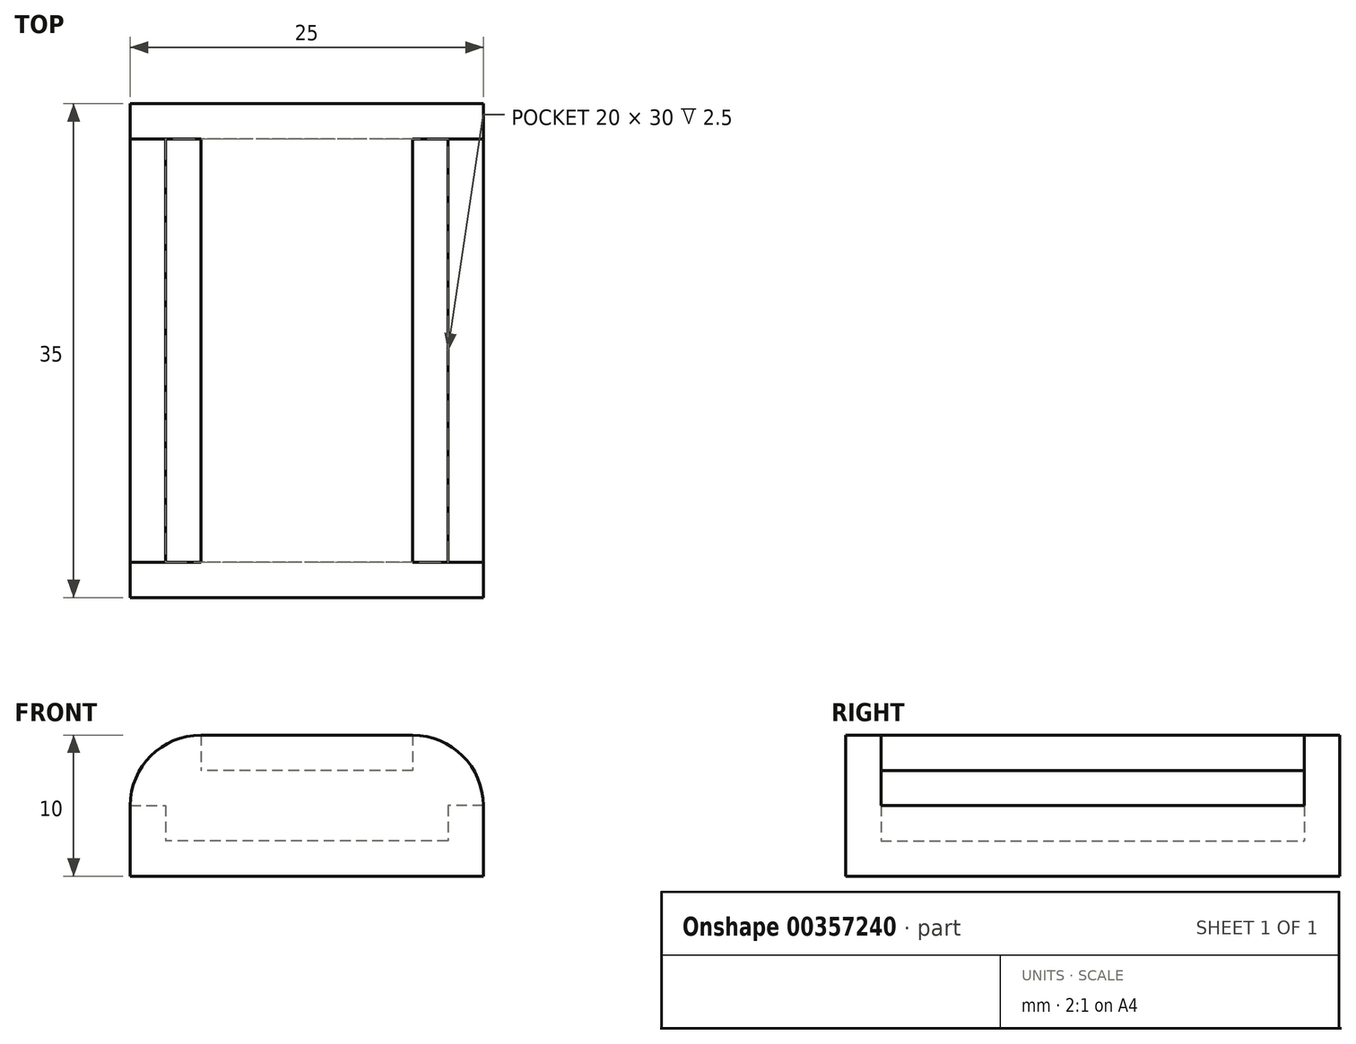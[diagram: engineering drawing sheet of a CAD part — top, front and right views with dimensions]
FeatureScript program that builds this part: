
annotation { "Feature Type Name" : "Feature", "Feature Type Description" : "" }
export const myFeature = defineFeature(function(context is Context, id is Id, definition is map)
    precondition{}
    {
        {
            var Q0;
            Q0=qCreatedBy(makeId("Top.planeOp"),FACE);
            var sketch = newSketch(context, id + "F0", { "sketchPlane" : qUnion([Q0])});
            skLineSegment(sketch, "E0.bottom", {"start": v(12.5, -17.5) * mm, "end": v(-12.5, -17.5) * mm});
            skLineSegment(sketch, "E0.top", {"start": v(12.5, 17.5) * mm, "end": v(-12.5, 17.5) * mm});
            skLineSegment(sketch, "E0.left", {"start": v(12.5, -17.5) * mm, "end": v(12.5, 17.5) * mm});
            skLineSegment(sketch, "E0.right", {"start": v(-12.5, -17.5) * mm, "end": v(-12.5, 17.5) * mm});
            skPoint(sketch, "E0.middle", {"position": v(0, 0) * mm});
            skSolve(sketch);
        }
        {
            var Q0;
            Q0 = qSketchRegion(id + "F0", true);
            extrude(context, id + "F1", {"entities" : qUnion([Q0]), "depth" : 5 * mm});
        }
        {
            var Q0;
            Q0=qCreatedBy(makeId("Top.planeOp"),FACE);
            var sketch = newSketch(context, id + "F2", { "sketchPlane" : qUnion([Q0])});
            skLineSegment(sketch, "E1.bottom", {"start": v(12.5, -17.5) * mm, "end": v(-12.5, -17.5) * mm});
            skLineSegment(sketch, "E1.top", {"start": v(12.5, 17.5) * mm, "end": v(-12.5, 17.5) * mm});
            skLineSegment(sketch, "E1.left", {"start": v(12.5, -17.5) * mm, "end": v(12.5, 17.5) * mm});
            skLineSegment(sketch, "E1.right", {"start": v(-12.5, -17.5) * mm, "end": v(-12.5, 17.5) * mm});
            skPoint(sketch, "E1.middle", {"position": v(0, 0) * mm});
            skSolve(sketch);
        }
        {
            var Q0;
            Q0 = qSketchRegion(id + "F2", true);
            extrude(context, id + "F3", {"entities" : qUnion([Q0]), "operationType" : NewBodyOperationType.ADD, "depth" : 10 * mm});
        }
        {
            var Q0;
            Q0=makeQuery(id+"F3.opExtrude","CAP_EDGE",EDGE,{"disambiguationData":[OSD([sQuery(id+"F2.wireOp",EDGE,"E1.right")])],"isStart":false});
            var Q1;
            Q1=makeQuery(id+"F3.opExtrude","CAP_EDGE",EDGE,{"disambiguationData":[OSD([sQuery(id+"F2.wireOp",EDGE,"E1.left")])],"isStart":false});
            fillet(context, id + "F4", {"entities" : qUnion([Q0, Q1]), "radius" : 5 * mm, "tangentPropagation" : true, "allowEdgeOverflow" : false});
        }
        {
            var Q0;
            Q0=makeQuery(id+"F4.opFillet","BLEND_FACE",FACE,{"disambiguationData":[OSD([sQuery(id+"F2.wireOp",EDGE,"E1.right")])]});
            var Q1;
            Q1=makeQuery(id+"F4.opFillet","BLEND_FACE",FACE,{"disambiguationData":[OSD([sQuery(id+"F2.wireOp",EDGE,"E1.left")])]});
            shell(context, id + "F5", {"entities" : qUnion([Q0, Q1]), "thickness" : 2.5 * mm});
        }
    });
